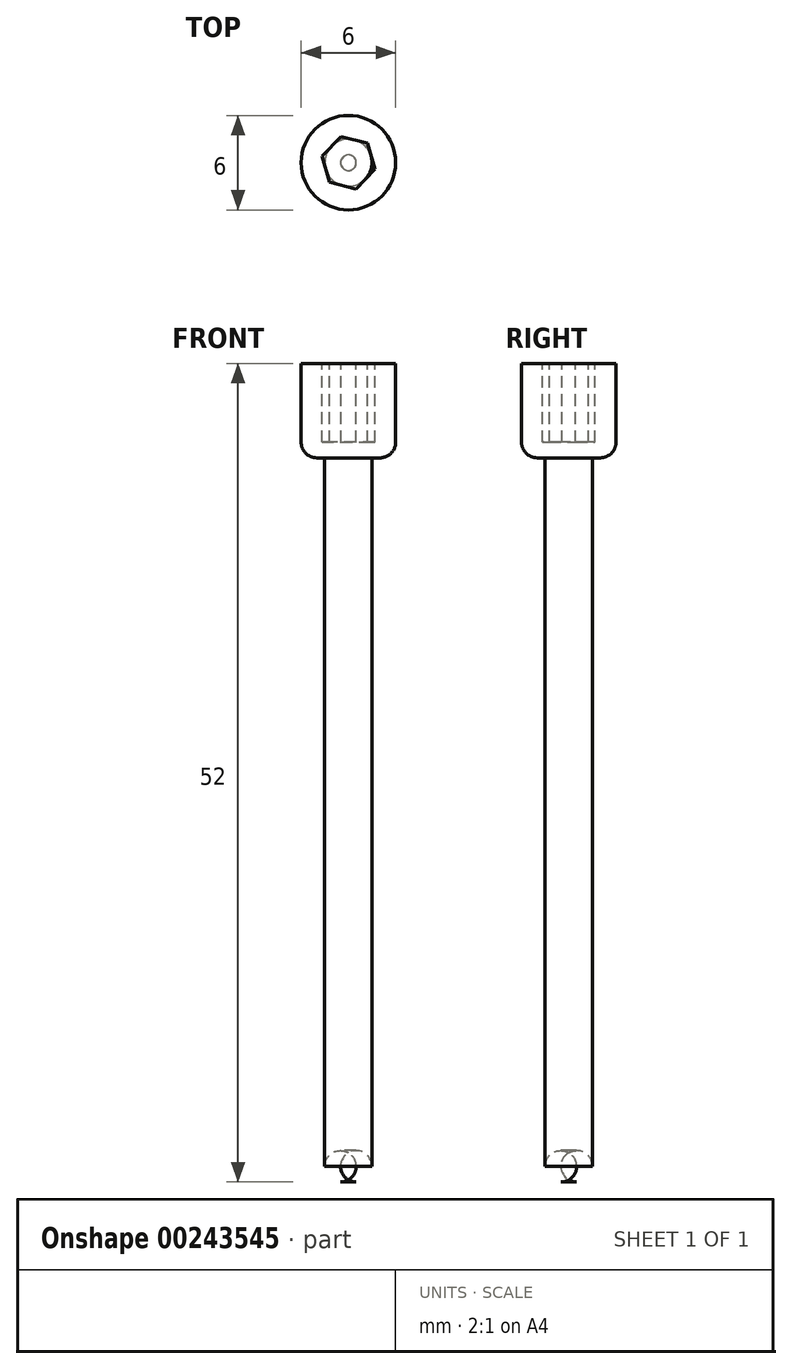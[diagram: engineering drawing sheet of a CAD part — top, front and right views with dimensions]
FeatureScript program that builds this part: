
annotation { "Feature Type Name" : "Feature", "Feature Type Description" : "" }
export const myFeature = defineFeature(function(context is Context, id is Id, definition is map)
    precondition{}
    {
        {
            var Q0;
            Q0=qCreatedBy(makeId("Top.planeOp"),FACE);
            var sketch = newSketch(context, id + "F0", { "sketchPlane" : qUnion([Q0])});
            skCircle(sketch, "E0", {"center": v(0, 0) * mm, "radius": 1.5 * mm});
            skSolve(sketch);
        }
        {
            var Q0;
            Q0=makeQuery(id+"F0.imprint","IMPRINT",FACE,{"disambiguationData":[TD([[makeQuery(id+"F0.imprint","IMPRINT",EDGE,{"derivedFrom":sQuery(id+"F0.wireOp",EDGE,"E0")}),1.0]])]});
            extrude(context, id + "F1", {"entities" : qUnion([Q0]), "depth" : 52 * mm});
        }
        {
            var Q0;
            Q0=makeQuery(id+"F1.opExtrude","CAP_FACE",FACE,{"disambiguationData":[OSD([sQuery(id+"F0.wireOp",EDGE,"E0")])],"isStart":false});
            var sketch = newSketch(context, id + "F2", { "sketchPlane" : qUnion([Q0])});
            skCircle(sketch, "E1", {"center": v(0, 0) * mm, "radius": 3 * mm});
            skSolve(sketch);
        }
        {
            var Q0;
            Q0=makeQuery(id+"F2.imprint","IMPRINT",FACE,{"disambiguationData":[TD([[makeQuery(id+"F2.imprint","IMPRINT",EDGE,{"derivedFrom":sQuery(id+"F2.wireOp",EDGE,"E1")}),1.0]])]});
            var Q1;
            Q1=makeQuery(id+"F2.imprint","IMPRINT",FACE,{"disambiguationData":[TD([[makeQuery(id+"F2.imprint","IMPRINT",EDGE,{"derivedFrom":makeQuery(id+"F1.opExtrude","CAP_EDGE",EDGE,{"disambiguationData":[OSD([sQuery(id+"F0.wireOp",EDGE,"E0")])],"isStart":false})}),1.0]])]});
            extrude(context, id + "F3", {"entities" : qUnion([Q0, Q1]), "operationType" : NewBodyOperationType.ADD, "oppositeDirection" : true, "depth" : 6 * mm});
        }
        {
            var Q0;
            Q0=makeQuery(id+"F3.boolean.opBoolean","MERGE",FACE,{"derivedFrom":[makeQuery(id+"F1.opExtrude","CAP_FACE",FACE,{"disambiguationData":[OSD([sQuery(id+"F0.wireOp",EDGE,"E0")])],"isStart":false}),makeQuery(id+"F3.opExtrude","CAP_FACE",FACE,{"disambiguationData":[OSD([sQuery(id+"F2.wireOp",EDGE,"E1")])],"isStart":true})]});
            var sketch = newSketch(context, id + "F4", { "sketchPlane" : qUnion([Q0])});
            skCircle(sketch, "E2.cCircle", {"center": v(0, 0) * mm, "radius": 1.5 * mm, "construction": true});
            skLineSegment(sketch, "E2.0", {"start": v(1.68, -0.42) * mm, "end": v(0.47, -1.67) * mm});
            skLineSegment(sketch, "E2.1", {"start": v(0.47, -1.67) * mm, "end": v(-1.2, -1.24) * mm});
            skLineSegment(sketch, "E2.2", {"start": v(-1.2, -1.24) * mm, "end": v(-1.68, 0.42) * mm});
            skLineSegment(sketch, "E2.3", {"start": v(-1.68, 0.42) * mm, "end": v(-0.47, 1.67) * mm});
            skLineSegment(sketch, "E2.4", {"start": v(-0.47, 1.67) * mm, "end": v(1.2, 1.24) * mm});
            skLineSegment(sketch, "E2.5", {"start": v(1.2, 1.24) * mm, "end": v(1.68, -0.42) * mm});
            skPoint(sketch, "E2.0.midPoint", {"position": v(1.08, -1.05) * mm});
            skSolve(sketch);
        }
        {
            var Q0;
            Q0=makeQuery(id+"F4.imprint","IMPRINT",FACE,{"disambiguationData":[TD([[makeQuery(id+"F4.imprint","IMPRINT",EDGE,{"derivedFrom":sQuery(id+"F4.wireOp",EDGE,"E2.0")}),-1.0]])]});
            extrude(context, id + "F5", {"entities" : qUnion([Q0]), "operationType" : NewBodyOperationType.REMOVE, "oppositeDirection" : true, "depth" : 5 * mm});
        }
        {
            var Q0;
            Q0=makeQuery(id+"F1.opExtrude","CAP_EDGE",EDGE,{"disambiguationData":[OSD([sQuery(id+"F0.wireOp",EDGE,"E0")])],"isStart":true});
            var Q1;
            Q1=makeQuery(id+"F3.opExtrude","CAP_EDGE",EDGE,{"disambiguationData":[OSD([sQuery(id+"F2.wireOp",EDGE,"E1")])],"isStart":false});
            fillet(context, id + "F6", {"entities" : qUnion([Q0, Q1]), "radius" : 1 * mm, "tangentPropagation" : true, "allowEdgeOverflow" : false});
        }
    });
